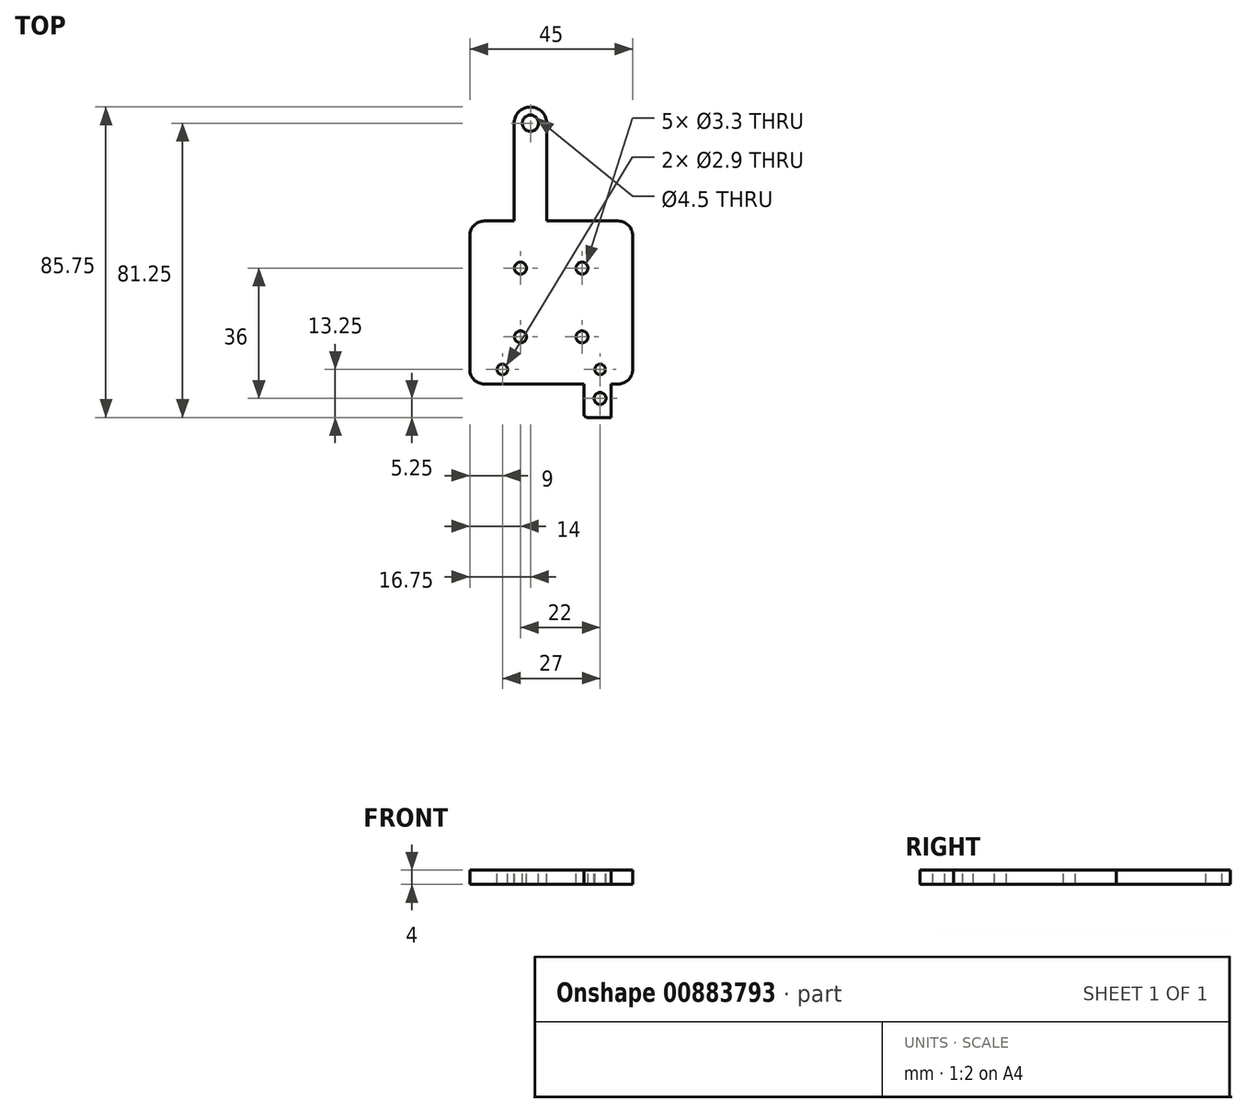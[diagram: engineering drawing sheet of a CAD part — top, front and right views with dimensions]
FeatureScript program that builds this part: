
annotation { "Feature Type Name" : "Feature", "Feature Type Description" : "" }
export const myFeature = defineFeature(function(context is Context, id is Id, definition is map)
    precondition{}
    {
        {
            var Q0;
            Q0=qCreatedBy(makeId("Top.planeOp"),FACE);
            var sketch = newSketch(context, id + "F0", { "sketchPlane" : qUnion([Q0])});
            skArc(sketch, "E0.0", {"start": v(-1.25, 49.5) * mm, "mid": v(-5.75, 54) * mm, "end": v(-10.25, 49.5) * mm});
            skLineSegment(sketch, "E0.1", {"start": v(-1.25, 49.5) * mm, "end": v(-1.25, 22.5) * mm});
            skLineSegment(sketch, "E0.2", {"start": v(18.5, 22.5) * mm, "end": v(-1.25, 22.5) * mm});
            skArc(sketch, "E0.4", {"start": v(22.5, 18.5) * mm, "mid": v(21.33, 21.33) * mm, "end": v(18.5, 22.5) * mm});
            skArc(sketch, "E0.6", {"start": v(18.5, -22.5) * mm, "mid": v(21.33, -21.33) * mm, "end": v(22.5, -18.5) * mm});
            skLineSegment(sketch, "E0.7", {"start": v(9, -30.75) * mm, "end": v(9, -22.5) * mm});
            skLineSegment(sketch, "E0.8", {"start": v(16.5, -31.75) * mm, "end": v(16.5, -22.5) * mm});
            skLineSegment(sketch, "E0.9", {"start": v(16.5, -31.75) * mm, "end": v(10, -31.75) * mm});
            skArc(sketch, "E0.10", {"start": v(9, -30.75) * mm, "mid": v(9.3, -31.46) * mm, "end": v(10, -31.75) * mm});
            skLineSegment(sketch, "E0.11", {"start": v(9, -22.5) * mm, "end": v(-18.5, -22.5) * mm});
            skArc(sketch, "E0.12", {"start": v(-18.5, -22.5) * mm, "mid": v(-21.33, -21.33) * mm, "end": v(-22.5, -18.5) * mm});
            skArc(sketch, "E0.15", {"start": v(-22.5, 18.5) * mm, "mid": v(-21.33, 21.33) * mm, "end": v(-18.5, 22.5) * mm});
            skLineSegment(sketch, "E0.16", {"start": v(-10.25, 22.5) * mm, "end": v(-18.5, 22.5) * mm});
            skLineSegment(sketch, "E0.17", {"start": v(-10.25, 22.5) * mm, "end": v(-10.25, 49.5) * mm});
            skLineSegment(sketch, "E0.18", {"start": v(18.5, -22.5) * mm, "end": v(16.5, -22.5) * mm});
            skLineSegment(sketch, "E1", {"start": v(22.5, 18.5) * mm, "end": v(22.5, -18.5) * mm});
            skLineSegment(sketch, "E2", {"start": v(-22.5, 18.5) * mm, "end": v(-22.5, -18.5) * mm});
            skLineSegment(sketch, "E3", {"start": v(-28.26, 0) * mm, "end": v(28.26, 0) * mm, "construction": true});
            skLineSegment(sketch, "E4", {"start": v(0, -31.05) * mm, "end": v(0, 25.93) * mm, "construction": true});
            skLineSegment(sketch, "E5", {"start": v(-5.75, 50.7) * mm, "end": v(-5.75, 35.81) * mm, "construction": true});
            skLineSegment(sketch, "E6", {"start": v(-10.99, 49.5) * mm, "end": v(-0.51, 49.5) * mm, "construction": true});
            skCircle(sketch, "E7", {"center": v(-5.75, 49.5) * mm, "radius": 2.25 * mm});
            skCircle(sketch, "E8", {"center": v(8.5, -9.5) * mm, "radius": 1.65 * mm});
            skCircle(sketch, "E9", {"center": v(8.5, 9.5) * mm, "radius": 1.65 * mm});
            skCircle(sketch, "E10", {"center": v(-8.5, 9.5) * mm, "radius": 1.65 * mm});
            skCircle(sketch, "E11", {"center": v(-8.5, -9.5) * mm, "radius": 1.65 * mm});
            skCircle(sketch, "E12", {"center": v(-13.5, -18.5) * mm, "radius": 1.45 * mm});
            skCircle(sketch, "E13", {"center": v(13.5, -18.5) * mm, "radius": 1.45 * mm});
            skCircle(sketch, "E14", {"center": v(13.5, -26.5) * mm, "radius": 1.65 * mm});
            skLineSegment(sketch, "E15", {"start": v(-8.5, -9.5) * mm, "end": v(-8.5, -18.5) * mm, "construction": true});
            skLineSegment(sketch, "E16", {"start": v(-8.5, -18.5) * mm, "end": v(-13.5, -18.5) * mm, "construction": true});
            skSolve(sketch);
        }
        {
            var Q0;
            Q0=makeQuery(id+"F0.imprint","IMPRINT",FACE,{"disambiguationData":[TD([[makeQuery(id+"F0.imprint","IMPRINT",EDGE,{"derivedFrom":sQuery(id+"F0.wireOp",EDGE,"E0.0")}),1.0]])]});
            extrude(context, id + "F1", {"entities" : qUnion([Q0]), "oppositeDirection" : true, "depth" : 4 * mm, "offsetDistance" : 25 * mm});
        }
    });
